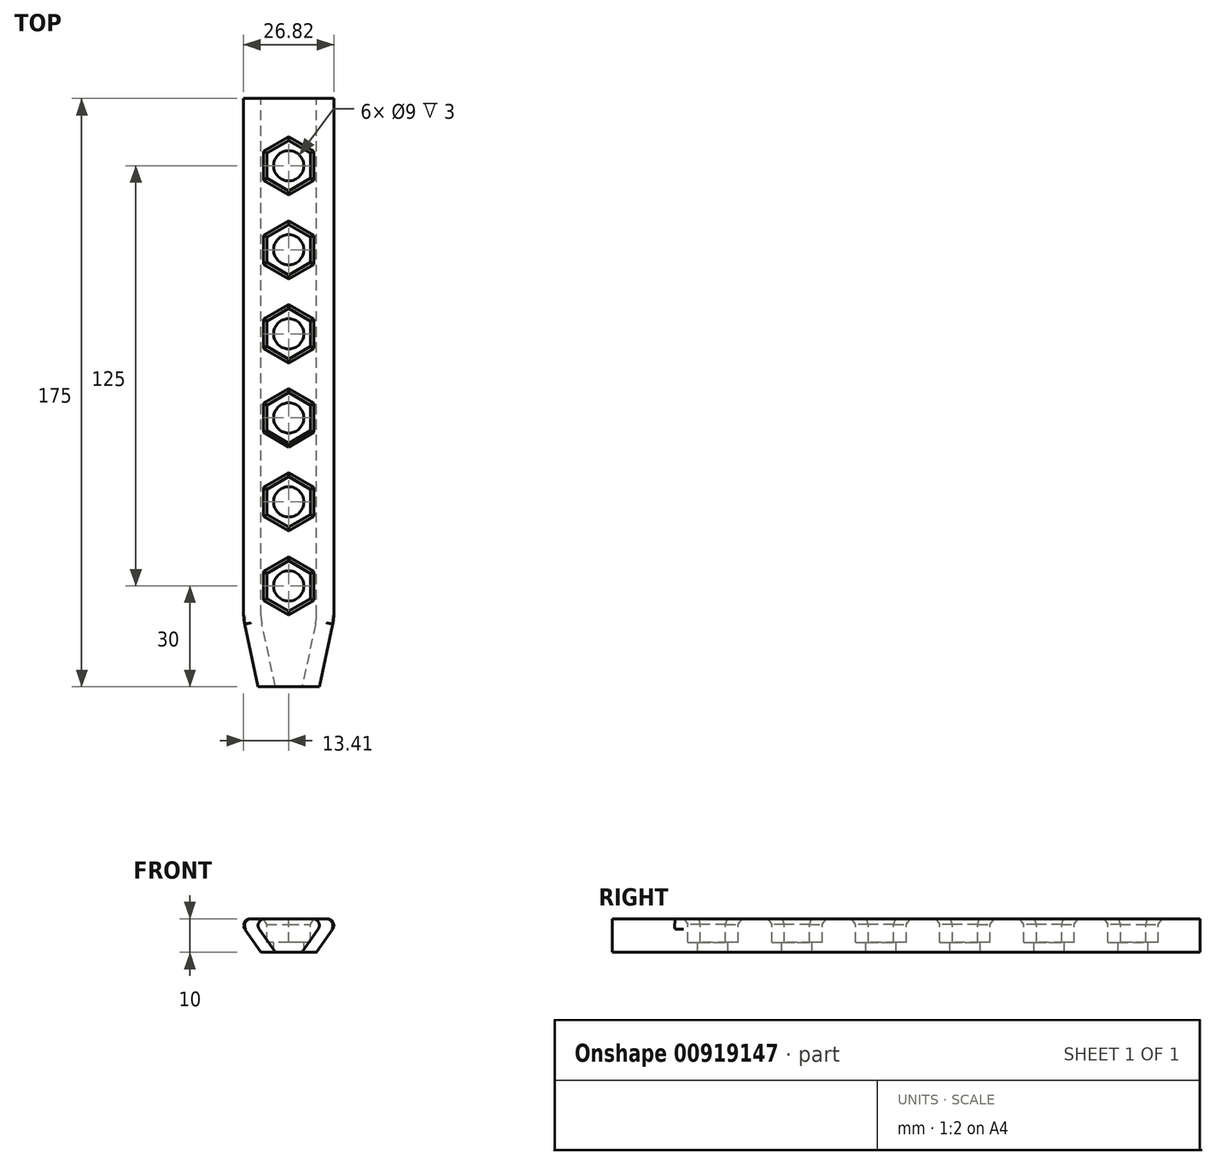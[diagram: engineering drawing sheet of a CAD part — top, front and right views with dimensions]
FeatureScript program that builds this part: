
annotation { "Feature Type Name" : "Feature", "Feature Type Description" : "" }
export const myFeature = defineFeature(function(context is Context, id is Id, definition is map)
    precondition{}
    {
        {
            var Q0;
            Q0=qCreatedBy(makeId("Front.planeOp"),FACE);
            var sketch = newSketch(context, id + "F0", { "sketchPlane" : qUnion([Q0])});
            skLineSegment(sketch, "E0", {"start": v(-8.25, 0) * mm, "end": v(8.25, 0) * mm});
            skLineSegment(sketch, "E1", {"start": v(8.25, 0) * mm, "end": v(15.25, 10) * mm});
            skLineSegment(sketch, "E2", {"start": v(15.25, 10) * mm, "end": v(-15.25, 10) * mm});
            skLineSegment(sketch, "E3", {"start": v(-15.25, 10) * mm, "end": v(-8.25, 0) * mm});
            skSolve(sketch);
        }
        {
            var Q0;
            Q0=makeQuery(id+"F0.imprint","IMPRINT",FACE,{"disambiguationData":[TD([[makeQuery(id+"F0.imprint","IMPRINT",EDGE,{"derivedFrom":sQuery(id+"F0.wireOp",EDGE,"E0")}),1.0]])]});
            extrude(context, id + "F1", {"entities" : qUnion([Q0]), "depth" : 175 * mm, "offsetDistance" : 25 * mm});
        }
        {
            var Q0;
            Q0=makeQuery(id+"F1.opExtrude","SWEPT_FACE",FACE,{"disambiguationData":[OSD([sQuery(id+"F0.wireOp",EDGE,"E2")])]});
            var sketch = newSketch(context, id + "F2", { "sketchPlane" : qUnion([Q0])});
            skLineSegment(sketch, "E4", {"start": v(0, 0) * mm, "end": v(0, -194.38) * mm, "construction": true});
            skCircle(sketch, "E5.cCircle", {"center": v(0, -20) * mm, "radius": 6.5 * mm, "construction": true});
            skLineSegment(sketch, "E5.0", {"start": v(6.5, -16.25) * mm, "end": v(6.5, -23.75) * mm});
            skLineSegment(sketch, "E5.1", {"start": v(6.5, -23.75) * mm, "end": v(0, -27.5) * mm});
            skLineSegment(sketch, "E5.2", {"start": v(0, -27.5) * mm, "end": v(-6.5, -23.75) * mm});
            skLineSegment(sketch, "E5.3", {"start": v(-6.5, -23.75) * mm, "end": v(-6.5, -16.25) * mm});
            skLineSegment(sketch, "E5.4", {"start": v(-6.5, -16.25) * mm, "end": v(0, -12.5) * mm});
            skLineSegment(sketch, "E5.5", {"start": v(0, -12.5) * mm, "end": v(6.5, -16.25) * mm});
            skPoint(sketch, "E5.0.midPoint", {"position": v(6.5, -20) * mm});
            skLineSegment(sketch, "E6.direction1", {"start": v(0, -27.5) * mm, "end": v(-25, -27.5) * mm, "construction": true});
            skLineSegment(sketch, "E6.direction2", {"start": v(0, -27.5) * mm, "end": v(0, -52.5) * mm, "construction": true});
            skLineSegment(sketch, "E7.0.1.0", {"start": v(-6.5, -48.75) * mm, "end": v(-6.5, -41.25) * mm});
            skLineSegment(sketch, "E7.0.1.1", {"start": v(-6.5, -41.25) * mm, "end": v(0, -37.5) * mm});
            skLineSegment(sketch, "E7.0.1.2", {"start": v(0, -37.5) * mm, "end": v(6.5, -41.25) * mm});
            skLineSegment(sketch, "E7.0.1.3", {"start": v(6.5, -41.25) * mm, "end": v(6.5, -48.75) * mm});
            skLineSegment(sketch, "E7.0.1.4", {"start": v(6.5, -48.75) * mm, "end": v(0, -52.5) * mm});
            skLineSegment(sketch, "E7.0.1.5", {"start": v(0, -52.5) * mm, "end": v(-6.5, -48.75) * mm});
            skLineSegment(sketch, "E7.0.2.0", {"start": v(-6.5, -73.75) * mm, "end": v(-6.5, -66.25) * mm});
            skLineSegment(sketch, "E7.0.2.1", {"start": v(-6.5, -66.25) * mm, "end": v(0, -62.5) * mm});
            skLineSegment(sketch, "E7.0.2.2", {"start": v(0, -62.5) * mm, "end": v(6.5, -66.25) * mm});
            skLineSegment(sketch, "E7.0.2.3", {"start": v(6.5, -66.25) * mm, "end": v(6.5, -73.75) * mm});
            skLineSegment(sketch, "E7.0.2.4", {"start": v(6.5, -73.75) * mm, "end": v(0, -77.5) * mm});
            skLineSegment(sketch, "E7.0.2.5", {"start": v(0, -77.5) * mm, "end": v(-6.5, -73.75) * mm});
            skLineSegment(sketch, "E7.0.3.0", {"start": v(-6.5, -98.75) * mm, "end": v(-6.5, -91.25) * mm});
            skLineSegment(sketch, "E7.0.3.1", {"start": v(-6.5, -91.25) * mm, "end": v(0, -87.5) * mm});
            skLineSegment(sketch, "E7.0.3.2", {"start": v(0, -87.5) * mm, "end": v(6.5, -91.25) * mm});
            skLineSegment(sketch, "E7.0.3.3", {"start": v(6.5, -91.25) * mm, "end": v(6.5, -98.75) * mm});
            skLineSegment(sketch, "E7.0.3.4", {"start": v(6.5, -98.75) * mm, "end": v(0, -102.5) * mm});
            skLineSegment(sketch, "E7.0.3.5", {"start": v(0, -102.5) * mm, "end": v(-6.5, -98.75) * mm});
            skLineSegment(sketch, "E7.0.4.0", {"start": v(-6.5, -123.75) * mm, "end": v(-6.5, -116.25) * mm});
            skLineSegment(sketch, "E7.0.4.1", {"start": v(-6.5, -116.25) * mm, "end": v(0, -112.5) * mm});
            skLineSegment(sketch, "E7.0.4.2", {"start": v(0, -112.5) * mm, "end": v(6.5, -116.25) * mm});
            skLineSegment(sketch, "E7.0.4.3", {"start": v(6.5, -116.25) * mm, "end": v(6.5, -123.75) * mm});
            skLineSegment(sketch, "E7.0.4.4", {"start": v(6.5, -123.75) * mm, "end": v(0, -127.5) * mm});
            skLineSegment(sketch, "E7.0.4.5", {"start": v(0, -127.5) * mm, "end": v(-6.5, -123.75) * mm});
            skLineSegment(sketch, "E7.0.5.0", {"start": v(-6.5, -148.75) * mm, "end": v(-6.5, -141.25) * mm});
            skLineSegment(sketch, "E7.0.5.1", {"start": v(-6.5, -141.25) * mm, "end": v(0, -137.5) * mm});
            skLineSegment(sketch, "E7.0.5.2", {"start": v(0, -137.5) * mm, "end": v(6.5, -141.25) * mm});
            skLineSegment(sketch, "E7.0.5.3", {"start": v(6.5, -141.25) * mm, "end": v(6.5, -148.75) * mm});
            skLineSegment(sketch, "E7.0.5.4", {"start": v(6.5, -148.75) * mm, "end": v(0, -152.5) * mm});
            skLineSegment(sketch, "E7.0.5.5", {"start": v(0, -152.5) * mm, "end": v(-6.5, -148.75) * mm});
            skLineSegment(sketch, "E7.direction1", {"start": v(-6.5, -23.75) * mm, "end": v(18.5, -23.75) * mm, "construction": true});
            skLineSegment(sketch, "E7.direction2", {"start": v(-6.5, -23.75) * mm, "end": v(-6.5, -48.75) * mm, "construction": true});
            skCircle(sketch, "E8", {"center": v(0, -20) * mm, "radius": 4.5 * mm});
            skCircle(sketch, "E9", {"center": v(11.63, -20) * mm, "radius": 0.68 * mm});
            skCircle(sketch, "E10.0.1.0", {"center": v(0, -45) * mm, "radius": 4.5 * mm});
            skCircle(sketch, "E10.0.2.0", {"center": v(0, -70) * mm, "radius": 4.5 * mm});
            skCircle(sketch, "E10.0.3.0", {"center": v(0, -95) * mm, "radius": 4.5 * mm});
            skCircle(sketch, "E10.0.4.0", {"center": v(0, -120) * mm, "radius": 4.5 * mm});
            skCircle(sketch, "E10.0.5.0", {"center": v(0, -145) * mm, "radius": 4.5 * mm});
            skLineSegment(sketch, "E10.direction1", {"start": v(0, -20) * mm, "end": v(25, -20) * mm, "construction": true});
            skLineSegment(sketch, "E10.direction2", {"start": v(0, -20) * mm, "end": v(0, -45) * mm, "construction": true});
            skSolve(sketch);
        }
        {
            var Q0;
            Q0=makeQuery(id+"F2.imprint","IMPRINT",FACE,{"disambiguationData":[TD([[makeQuery(id+"F2.imprint","IMPRINT",EDGE,{"derivedFrom":sQuery(id+"F2.wireOp",EDGE,"E5.0")}),-1.0]])]});
            var Q1;
            Q1=makeQuery(id+"F2.imprint","IMPRINT",FACE,{"disambiguationData":[TD([[makeQuery(id+"F2.imprint","IMPRINT",EDGE,{"derivedFrom":sQuery(id+"F2.wireOp",EDGE,"E7.0.1.0")}),-1.0]])]});
            var Q2;
            Q2=makeQuery(id+"F2.imprint","IMPRINT",FACE,{"disambiguationData":[TD([[makeQuery(id+"F2.imprint","IMPRINT",EDGE,{"derivedFrom":sQuery(id+"F2.wireOp",EDGE,"E7.0.2.0")}),-1.0]])]});
            var Q3;
            Q3=makeQuery(id+"F2.imprint","IMPRINT",FACE,{"disambiguationData":[TD([[makeQuery(id+"F2.imprint","IMPRINT",EDGE,{"derivedFrom":sQuery(id+"F2.wireOp",EDGE,"E7.0.3.0")}),-1.0]])]});
            var Q4;
            Q4=makeQuery(id+"F2.imprint","IMPRINT",FACE,{"disambiguationData":[TD([[makeQuery(id+"F2.imprint","IMPRINT",EDGE,{"derivedFrom":sQuery(id+"F2.wireOp",EDGE,"E7.0.4.0")}),-1.0]])]});
            var Q5;
            Q5=makeQuery(id+"F2.imprint","IMPRINT",FACE,{"disambiguationData":[TD([[makeQuery(id+"F2.imprint","IMPRINT",EDGE,{"derivedFrom":sQuery(id+"F2.wireOp",EDGE,"E7.0.5.0")}),-1.0]])]});
            extrude(context, id + "F3", {"entities" : qUnion([Q0, Q1, Q2, Q3, Q4, Q5]), "operationType" : NewBodyOperationType.REMOVE, "oppositeDirection" : true, "depth" : 7 * mm, "offsetDistance" : 25 * mm});
        }
        {
            var Q0;
            Q0=makeQuery(id+"F3.boolean.opBoolean","SPLIT",FACE,{"disambiguationData":[TD([makeQuery(id+"F3.opExtrude","SWEPT_FACE",FACE,{"disambiguationData":[OSD([sQuery(id+"F2.wireOp",EDGE,"E8")])]})])],"derivedFrom":makeQuery(id+"F1.opExtrude","SWEPT_FACE",FACE,{"disambiguationData":[OSD([sQuery(id+"F0.wireOp",EDGE,"E2")])]})});
            var Q1;
            Q1=makeQuery(id+"F3.boolean.opBoolean","SPLIT",FACE,{"disambiguationData":[TD([makeQuery(id+"F3.opExtrude","SWEPT_FACE",FACE,{"disambiguationData":[OSD([sQuery(id+"F2.wireOp",EDGE,"E10.0.1.0")])]})])],"derivedFrom":makeQuery(id+"F1.opExtrude","SWEPT_FACE",FACE,{"disambiguationData":[OSD([sQuery(id+"F0.wireOp",EDGE,"E2")])]})});
            var Q2;
            Q2=makeQuery(id+"F3.boolean.opBoolean","SPLIT",FACE,{"disambiguationData":[TD([makeQuery(id+"F3.opExtrude","SWEPT_FACE",FACE,{"disambiguationData":[OSD([sQuery(id+"F2.wireOp",EDGE,"E10.0.2.0")])]})])],"derivedFrom":makeQuery(id+"F1.opExtrude","SWEPT_FACE",FACE,{"disambiguationData":[OSD([sQuery(id+"F0.wireOp",EDGE,"E2")])]})});
            var Q3;
            Q3=makeQuery(id+"F3.boolean.opBoolean","SPLIT",FACE,{"disambiguationData":[TD([makeQuery(id+"F3.opExtrude","SWEPT_FACE",FACE,{"disambiguationData":[OSD([sQuery(id+"F2.wireOp",EDGE,"E10.0.3.0")])]})])],"derivedFrom":makeQuery(id+"F1.opExtrude","SWEPT_FACE",FACE,{"disambiguationData":[OSD([sQuery(id+"F0.wireOp",EDGE,"E2")])]})});
            var Q4;
            Q4=makeQuery(id+"F3.boolean.opBoolean","SPLIT",FACE,{"disambiguationData":[TD([makeQuery(id+"F3.opExtrude","SWEPT_FACE",FACE,{"disambiguationData":[OSD([sQuery(id+"F2.wireOp",EDGE,"E10.0.4.0")])]})])],"derivedFrom":makeQuery(id+"F1.opExtrude","SWEPT_FACE",FACE,{"disambiguationData":[OSD([sQuery(id+"F0.wireOp",EDGE,"E2")])]})});
            var Q5;
            Q5=makeQuery(id+"F3.boolean.opBoolean","SPLIT",FACE,{"disambiguationData":[TD([makeQuery(id+"F3.opExtrude","SWEPT_FACE",FACE,{"disambiguationData":[OSD([sQuery(id+"F2.wireOp",EDGE,"E10.0.5.0")])]})])],"derivedFrom":makeQuery(id+"F1.opExtrude","SWEPT_FACE",FACE,{"disambiguationData":[OSD([sQuery(id+"F0.wireOp",EDGE,"E2")])]})});
            extrude(context, id + "F4", {"entities" : qUnion([Q0, Q1, Q2, Q3, Q4, Q5]), "operationType" : NewBodyOperationType.REMOVE, "oppositeDirection" : true, "depth" : 25 * mm, "offsetDistance" : 25 * mm});
        }
        {
            var Q0;
            Q0=makeQuery(id+"F3.boolean.opBoolean","COPY",EDGE,{"derivedFrom":makeQuery(id+"F3.opExtrude","CAP_EDGE",EDGE,{"disambiguationData":[OSD([sQuery(id+"F2.wireOp",EDGE,"E7.0.5.0")])],"isStart":true})});
            var Q1;
            Q1=makeQuery(id+"F3.boolean.opBoolean","COPY",EDGE,{"derivedFrom":makeQuery(id+"F3.opExtrude","CAP_EDGE",EDGE,{"disambiguationData":[OSD([sQuery(id+"F2.wireOp",EDGE,"E7.0.5.1")])],"isStart":true})});
            var Q2;
            Q2=makeQuery(id+"F3.boolean.opBoolean","COPY",EDGE,{"derivedFrom":makeQuery(id+"F3.opExtrude","CAP_EDGE",EDGE,{"disambiguationData":[OSD([sQuery(id+"F2.wireOp",EDGE,"E7.0.5.5")])],"isStart":true})});
            var Q3;
            Q3=makeQuery(id+"F3.boolean.opBoolean","COPY",EDGE,{"derivedFrom":makeQuery(id+"F3.opExtrude","CAP_EDGE",EDGE,{"disambiguationData":[OSD([sQuery(id+"F2.wireOp",EDGE,"E7.0.5.4")])],"isStart":true})});
            var Q4;
            Q4=makeQuery(id+"F3.boolean.opBoolean","COPY",EDGE,{"derivedFrom":makeQuery(id+"F3.opExtrude","CAP_EDGE",EDGE,{"disambiguationData":[OSD([sQuery(id+"F2.wireOp",EDGE,"E7.0.5.3")])],"isStart":true})});
            var Q5;
            Q5=makeQuery(id+"F3.boolean.opBoolean","COPY",EDGE,{"derivedFrom":makeQuery(id+"F3.opExtrude","CAP_EDGE",EDGE,{"disambiguationData":[OSD([sQuery(id+"F2.wireOp",EDGE,"E7.0.5.2")])],"isStart":true})});
            var Q6;
            Q6=makeQuery(id+"F3.boolean.opBoolean","COPY",EDGE,{"derivedFrom":makeQuery(id+"F3.opExtrude","CAP_EDGE",EDGE,{"disambiguationData":[OSD([sQuery(id+"F2.wireOp",EDGE,"E7.0.4.5")])],"isStart":true})});
            var Q7;
            Q7=makeQuery(id+"F3.boolean.opBoolean","COPY",EDGE,{"derivedFrom":makeQuery(id+"F3.opExtrude","CAP_EDGE",EDGE,{"disambiguationData":[OSD([sQuery(id+"F2.wireOp",EDGE,"E7.0.4.0")])],"isStart":true})});
            var Q8;
            Q8=makeQuery(id+"F3.boolean.opBoolean","COPY",EDGE,{"derivedFrom":makeQuery(id+"F3.opExtrude","CAP_EDGE",EDGE,{"disambiguationData":[OSD([sQuery(id+"F2.wireOp",EDGE,"E7.0.4.1")])],"isStart":true})});
            var Q9;
            Q9=makeQuery(id+"F3.boolean.opBoolean","COPY",EDGE,{"derivedFrom":makeQuery(id+"F3.opExtrude","CAP_EDGE",EDGE,{"disambiguationData":[OSD([sQuery(id+"F2.wireOp",EDGE,"E7.0.4.2")])],"isStart":true})});
            var Q10;
            Q10=makeQuery(id+"F3.boolean.opBoolean","COPY",EDGE,{"derivedFrom":makeQuery(id+"F3.opExtrude","CAP_EDGE",EDGE,{"disambiguationData":[OSD([sQuery(id+"F2.wireOp",EDGE,"E7.0.4.3")])],"isStart":true})});
            var Q11;
            Q11=makeQuery(id+"F3.boolean.opBoolean","COPY",EDGE,{"derivedFrom":makeQuery(id+"F3.opExtrude","CAP_EDGE",EDGE,{"disambiguationData":[OSD([sQuery(id+"F2.wireOp",EDGE,"E7.0.4.4")])],"isStart":true})});
            var Q12;
            Q12=makeQuery(id+"F3.boolean.opBoolean","COPY",EDGE,{"derivedFrom":makeQuery(id+"F3.opExtrude","CAP_EDGE",EDGE,{"disambiguationData":[OSD([sQuery(id+"F2.wireOp",EDGE,"E7.0.3.0")])],"isStart":true})});
            var Q13;
            Q13=makeQuery(id+"F3.boolean.opBoolean","COPY",EDGE,{"derivedFrom":makeQuery(id+"F3.opExtrude","CAP_EDGE",EDGE,{"disambiguationData":[OSD([sQuery(id+"F2.wireOp",EDGE,"E7.0.3.1")])],"isStart":true})});
            var Q14;
            Q14=makeQuery(id+"F3.boolean.opBoolean","COPY",EDGE,{"derivedFrom":makeQuery(id+"F3.opExtrude","CAP_EDGE",EDGE,{"disambiguationData":[OSD([sQuery(id+"F2.wireOp",EDGE,"E7.0.3.2")])],"isStart":true})});
            var Q15;
            Q15=makeQuery(id+"F3.boolean.opBoolean","COPY",EDGE,{"derivedFrom":makeQuery(id+"F3.opExtrude","CAP_EDGE",EDGE,{"disambiguationData":[OSD([sQuery(id+"F2.wireOp",EDGE,"E7.0.3.3")])],"isStart":true})});
            var Q16;
            Q16=makeQuery(id+"F3.boolean.opBoolean","COPY",EDGE,{"derivedFrom":makeQuery(id+"F3.opExtrude","CAP_EDGE",EDGE,{"disambiguationData":[OSD([sQuery(id+"F2.wireOp",EDGE,"E7.0.3.4")])],"isStart":true})});
            var Q17;
            Q17=makeQuery(id+"F3.boolean.opBoolean","COPY",EDGE,{"derivedFrom":makeQuery(id+"F3.opExtrude","CAP_EDGE",EDGE,{"disambiguationData":[OSD([sQuery(id+"F2.wireOp",EDGE,"E7.0.3.5")])],"isStart":true})});
            var Q18;
            Q18=makeQuery(id+"F3.boolean.opBoolean","COPY",EDGE,{"derivedFrom":makeQuery(id+"F3.opExtrude","CAP_EDGE",EDGE,{"disambiguationData":[OSD([sQuery(id+"F2.wireOp",EDGE,"E7.0.2.5")])],"isStart":true})});
            var Q19;
            Q19=makeQuery(id+"F3.boolean.opBoolean","COPY",EDGE,{"derivedFrom":makeQuery(id+"F3.opExtrude","CAP_EDGE",EDGE,{"disambiguationData":[OSD([sQuery(id+"F2.wireOp",EDGE,"E7.0.2.0")])],"isStart":true})});
            var Q20;
            Q20=makeQuery(id+"F3.boolean.opBoolean","COPY",EDGE,{"derivedFrom":makeQuery(id+"F3.opExtrude","CAP_EDGE",EDGE,{"disambiguationData":[OSD([sQuery(id+"F2.wireOp",EDGE,"E7.0.2.1")])],"isStart":true})});
            var Q21;
            Q21=makeQuery(id+"F3.boolean.opBoolean","COPY",EDGE,{"derivedFrom":makeQuery(id+"F3.opExtrude","CAP_EDGE",EDGE,{"disambiguationData":[OSD([sQuery(id+"F2.wireOp",EDGE,"E7.0.2.2")])],"isStart":true})});
            var Q22;
            Q22=makeQuery(id+"F3.boolean.opBoolean","COPY",EDGE,{"derivedFrom":makeQuery(id+"F3.opExtrude","CAP_EDGE",EDGE,{"disambiguationData":[OSD([sQuery(id+"F2.wireOp",EDGE,"E7.0.2.3")])],"isStart":true})});
            var Q23;
            Q23=makeQuery(id+"F3.boolean.opBoolean","COPY",EDGE,{"derivedFrom":makeQuery(id+"F3.opExtrude","CAP_EDGE",EDGE,{"disambiguationData":[OSD([sQuery(id+"F2.wireOp",EDGE,"E7.0.2.4")])],"isStart":true})});
            var Q24;
            Q24=makeQuery(id+"F3.boolean.opBoolean","COPY",EDGE,{"derivedFrom":makeQuery(id+"F3.opExtrude","CAP_EDGE",EDGE,{"disambiguationData":[OSD([sQuery(id+"F2.wireOp",EDGE,"E7.0.1.0")])],"isStart":true})});
            var Q25;
            Q25=makeQuery(id+"F3.boolean.opBoolean","COPY",EDGE,{"derivedFrom":makeQuery(id+"F3.opExtrude","CAP_EDGE",EDGE,{"disambiguationData":[OSD([sQuery(id+"F2.wireOp",EDGE,"E7.0.1.1")])],"isStart":true})});
            var Q26;
            Q26=makeQuery(id+"F3.boolean.opBoolean","COPY",EDGE,{"derivedFrom":makeQuery(id+"F3.opExtrude","CAP_EDGE",EDGE,{"disambiguationData":[OSD([sQuery(id+"F2.wireOp",EDGE,"E7.0.1.2")])],"isStart":true})});
            var Q27;
            Q27=makeQuery(id+"F3.boolean.opBoolean","COPY",EDGE,{"derivedFrom":makeQuery(id+"F3.opExtrude","CAP_EDGE",EDGE,{"disambiguationData":[OSD([sQuery(id+"F2.wireOp",EDGE,"E7.0.1.3")])],"isStart":true})});
            var Q28;
            Q28=makeQuery(id+"F3.boolean.opBoolean","COPY",EDGE,{"derivedFrom":makeQuery(id+"F3.opExtrude","CAP_EDGE",EDGE,{"disambiguationData":[OSD([sQuery(id+"F2.wireOp",EDGE,"E7.0.1.4")])],"isStart":true})});
            var Q29;
            Q29=makeQuery(id+"F3.boolean.opBoolean","COPY",EDGE,{"derivedFrom":makeQuery(id+"F3.opExtrude","CAP_EDGE",EDGE,{"disambiguationData":[OSD([sQuery(id+"F2.wireOp",EDGE,"E7.0.1.5")])],"isStart":true})});
            var Q30;
            Q30=makeQuery(id+"F3.boolean.opBoolean","COPY",EDGE,{"derivedFrom":makeQuery(id+"F3.opExtrude","CAP_EDGE",EDGE,{"disambiguationData":[OSD([sQuery(id+"F2.wireOp",EDGE,"E5.2")])],"isStart":true})});
            var Q31;
            Q31=makeQuery(id+"F3.boolean.opBoolean","COPY",EDGE,{"derivedFrom":makeQuery(id+"F3.opExtrude","CAP_EDGE",EDGE,{"disambiguationData":[OSD([sQuery(id+"F2.wireOp",EDGE,"E5.3")])],"isStart":true})});
            var Q32;
            Q32=makeQuery(id+"F3.boolean.opBoolean","COPY",EDGE,{"derivedFrom":makeQuery(id+"F3.opExtrude","CAP_EDGE",EDGE,{"disambiguationData":[OSD([sQuery(id+"F2.wireOp",EDGE,"E5.4")])],"isStart":true})});
            var Q33;
            Q33=makeQuery(id+"F3.boolean.opBoolean","COPY",EDGE,{"derivedFrom":makeQuery(id+"F3.opExtrude","CAP_EDGE",EDGE,{"disambiguationData":[OSD([sQuery(id+"F2.wireOp",EDGE,"E5.5")])],"isStart":true})});
            var Q34;
            Q34=makeQuery(id+"F3.boolean.opBoolean","COPY",EDGE,{"derivedFrom":makeQuery(id+"F3.opExtrude","CAP_EDGE",EDGE,{"disambiguationData":[OSD([sQuery(id+"F2.wireOp",EDGE,"E5.0")])],"isStart":true})});
            var Q35;
            Q35=makeQuery(id+"F3.boolean.opBoolean","COPY",EDGE,{"derivedFrom":makeQuery(id+"F3.opExtrude","CAP_EDGE",EDGE,{"disambiguationData":[OSD([sQuery(id+"F2.wireOp",EDGE,"E5.1")])],"isStart":true})});
            chamfer(context, id + "F5", {"entities" : qUnion([Q0, Q1, Q2, Q3, Q4, Q5, Q6, Q7, Q8, Q9, Q10, Q11, Q12, Q13, Q14, Q15, Q16, Q17, Q18, Q19, Q20, Q21, Q22, Q23, Q24, Q25, Q26, Q27, Q28, Q29, Q30, Q31, Q32, Q33, Q34, Q35]), "chamferType" : ChamferType.OFFSET_ANGLE, "width" : 1 * mm, "oppositeDirection" : false, "angle" : 60 * degree, "tangentPropagation" : true});
        }
        {
            var Q0;
            Q0=makeQuery(id+"F1.opExtrude","CAP_EDGE",EDGE,{"disambiguationData":[OSD([sQuery(id+"F0.wireOp",EDGE,"E3")])],"isStart":false});
            var Q1;
            Q1=makeQuery(id+"F1.opExtrude","CAP_EDGE",EDGE,{"disambiguationData":[OSD([sQuery(id+"F0.wireOp",EDGE,"E1")])],"isStart":false});
            chamfer(context, id + "F6", {"entities" : qUnion([Q0, Q1]), "chamferType" : ChamferType.OFFSET_ANGLE, "width" : 20 * mm, "oppositeDirection" : true, "angle" : 10 * degree, "tangentPropagation" : true});
        }
        {
            var Q0;
            {var subQ0=sQuery(id+"F0.wireOp",EDGE,"E3");Q0=makeQuery(id+"F6.opChamfer","BLEND_EDGE",EDGE,{"blendedFrom":[makeQuery(id+"F1.opExtrude","CAP_EDGE",EDGE,{"disambiguationData":[OSD([subQ0])],"isStart":false}),makeQuery(id+"F1.opExtrude","SWEPT_FACE",FACE,{"disambiguationData":[OSD([subQ0])]})],"blendedInto":[makeQuery(id+"F1.opExtrude","SWEPT_FACE",FACE,{"disambiguationData":[OSD([subQ0])]})]});}
            var Q1;
            {var subQ0=sQuery(id+"F0.wireOp",EDGE,"E1");Q1=makeQuery(id+"F6.opChamfer","BLEND_EDGE",EDGE,{"blendedFrom":[makeQuery(id+"F1.opExtrude","CAP_EDGE",EDGE,{"disambiguationData":[OSD([subQ0])],"isStart":false}),makeQuery(id+"F1.opExtrude","SWEPT_FACE",FACE,{"disambiguationData":[OSD([subQ0])]})],"blendedInto":[makeQuery(id+"F1.opExtrude","SWEPT_FACE",FACE,{"disambiguationData":[OSD([subQ0])]})]});}
            fillet(context, id + "F7", {"entities" : qUnion([Q0, Q1]), "radius" : 15 * mm, "tangentPropagation" : true, "allowEdgeOverflow" : false});
        }
        {
            var Q0;
            {var subQ1=sQuery(id+"F0.wireOp",EDGE,"E1");var subQ2=sQuery(id+"F0.wireOp",EDGE,"E2");Q0=makeQuery(id+"F6.opChamfer","BLEND_EDGE",EDGE,{"blendedFrom":[makeQuery(id+"F1.opExtrude","CAP_EDGE",EDGE,{"disambiguationData":[OSD([subQ1])],"isStart":false}),makeQuery(id+"F3.boolean.opBoolean","SPLIT",FACE,{"disambiguationData":[TD([makeQuery(id+"F1.opExtrude","SWEPT_FACE",FACE,{"disambiguationData":[OSD([subQ1])]})])],"derivedFrom":makeQuery(id+"F1.opExtrude","SWEPT_FACE",FACE,{"disambiguationData":[OSD([subQ2])]})})],"blendedInto":[makeQuery(id+"F3.boolean.opBoolean","SPLIT",FACE,{"disambiguationData":[TD([makeQuery(id+"F1.opExtrude","SWEPT_FACE",FACE,{"disambiguationData":[OSD([subQ1])]})])],"derivedFrom":makeQuery(id+"F1.opExtrude","SWEPT_FACE",FACE,{"disambiguationData":[OSD([subQ2])]})})]});}
            var Q1;
            {var subQ0=sQuery(id+"F0.wireOp",EDGE,"E3");var subQ1=sQuery(id+"F0.wireOp",EDGE,"E1");var subQ2=sQuery(id+"F0.wireOp",EDGE,"E2");Q1=makeQuery(id+"F6.opChamfer","BLEND_EDGE",EDGE,{"blendedFrom":[makeQuery(id+"F1.opExtrude","CAP_EDGE",EDGE,{"disambiguationData":[OSD([subQ0])],"isStart":false}),makeQuery(id+"F3.boolean.opBoolean","SPLIT",FACE,{"disambiguationData":[TD([makeQuery(id+"F1.opExtrude","SWEPT_FACE",FACE,{"disambiguationData":[OSD([subQ1])]})])],"derivedFrom":makeQuery(id+"F1.opExtrude","SWEPT_FACE",FACE,{"disambiguationData":[OSD([subQ2])]})})],"blendedInto":[makeQuery(id+"F3.boolean.opBoolean","SPLIT",FACE,{"disambiguationData":[TD([makeQuery(id+"F1.opExtrude","SWEPT_FACE",FACE,{"disambiguationData":[OSD([subQ1])]})])],"derivedFrom":makeQuery(id+"F1.opExtrude","SWEPT_FACE",FACE,{"disambiguationData":[OSD([subQ2])]})})]});}
            fillet(context, id + "F8", {"entities" : qUnion([Q0, Q1]), "radius" : 2 * mm, "tangentPropagation" : true, "allowEdgeOverflow" : false});
        }
    });
